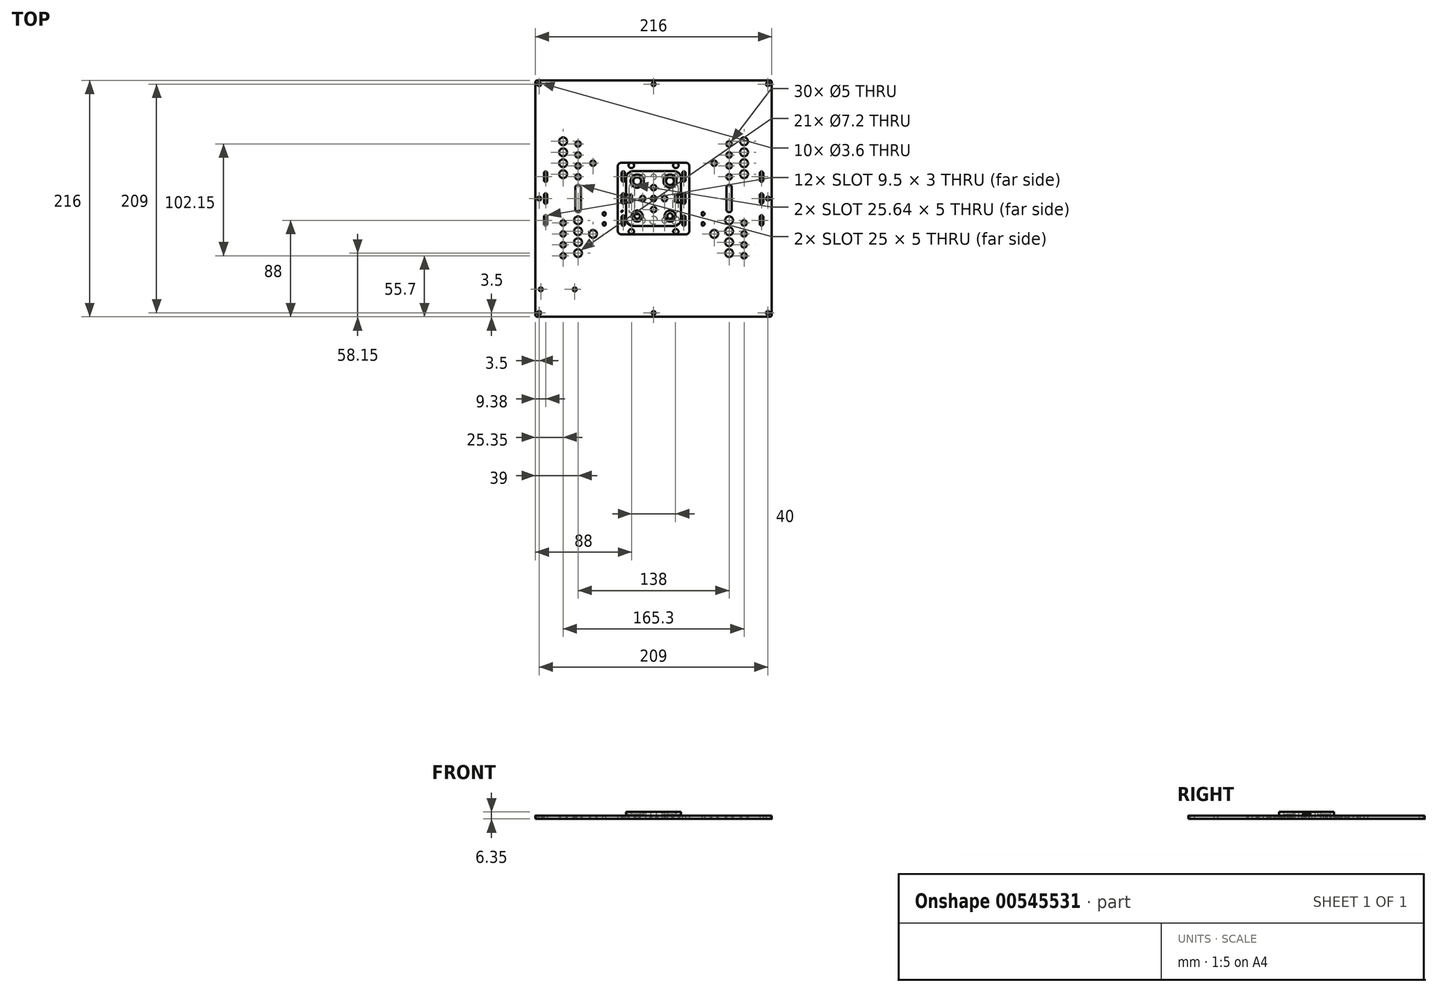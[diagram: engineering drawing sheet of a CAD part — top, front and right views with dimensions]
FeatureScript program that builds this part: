
annotation { "Feature Type Name" : "Feature", "Feature Type Description" : "" }
export const myFeature = defineFeature(function(context is Context, id is Id, definition is map)
    precondition{}
    {
        {
            var Q0;
            Q0=qCreatedBy(makeId("Top.planeOp"),FACE);
            var sketch = newSketch(context, id + "F0", { "sketchPlane" : qUnion([Q0])});
            skLineSegment(sketch, "E0.bottom", {"start": v(-106.25, 108) * mm, "end": v(106.25, 108) * mm});
            skLineSegment(sketch, "E0.top", {"start": v(-106.25, -108) * mm, "end": v(106.25, -108) * mm});
            skLineSegment(sketch, "E0.left", {"start": v(-108, 106.25) * mm, "end": v(-108, -106.25) * mm});
            skLineSegment(sketch, "E0.right", {"start": v(108, 106.25) * mm, "end": v(108, -106.25) * mm});
            skPoint(sketch, "E0.middle", {"position": v(0, 0) * mm});
            skPoint(sketch, "E1.visualSharp", {"position": v(-108, 108) * mm});
            skArc(sketch, "E1.filletArc", {"start": v(-106.25, 108) * mm, "mid": v(-107.49, 107.49) * mm, "end": v(-108, 106.25) * mm});
            skPoint(sketch, "E2.visualSharp", {"position": v(108, 108) * mm});
            skArc(sketch, "E2.filletArc", {"start": v(108, 106.25) * mm, "mid": v(107.49, 107.49) * mm, "end": v(106.25, 108) * mm});
            skPoint(sketch, "E3.visualSharp", {"position": v(108, -108) * mm});
            skArc(sketch, "E3.filletArc", {"start": v(106.25, -108) * mm, "mid": v(107.49, -107.49) * mm, "end": v(108, -106.25) * mm});
            skPoint(sketch, "E4.visualSharp", {"position": v(-108, -108) * mm});
            skArc(sketch, "E4.filletArc", {"start": v(-108, -106.25) * mm, "mid": v(-107.49, -107.49) * mm, "end": v(-106.25, -108) * mm});
            skCircle(sketch, "E5", {"center": v(-104.5, -104.5) * mm, "radius": 1.8 * mm});
            skCircle(sketch, "E6.0.1.0", {"center": v(-104.5, 0) * mm, "radius": 1.8 * mm});
            skCircle(sketch, "E6.0.2.0", {"center": v(-104.5, 104.5) * mm, "radius": 1.8 * mm});
            skCircle(sketch, "E6.1.0.0", {"center": v(0, -104.5) * mm, "radius": 1.8 * mm});
            skCircle(sketch, "E6.1.1.0", {"center": v(0, 0) * mm, "radius": 1.8 * mm});
            skCircle(sketch, "E6.1.2.0", {"center": v(0, 104.5) * mm, "radius": 1.8 * mm});
            skCircle(sketch, "E6.2.0.0", {"center": v(104.5, -104.5) * mm, "radius": 1.8 * mm});
            skCircle(sketch, "E6.2.1.0", {"center": v(104.5, 0) * mm, "radius": 1.8 * mm});
            skCircle(sketch, "E6.2.2.0", {"center": v(104.5, 104.5) * mm, "radius": 1.8 * mm});
            skLineSegment(sketch, "E6.direction1", {"start": v(-104.5, -104.5) * mm, "end": v(0, -104.5) * mm, "construction": true});
            skLineSegment(sketch, "E6.direction2", {"start": v(-104.5, -104.5) * mm, "end": v(-104.5, 0) * mm, "construction": true});
            skLineSegment(sketch, "E7", {"start": v(0, 0) * mm, "end": v(-30, 0) * mm, "construction": true});
            skLineSegment(sketch, "E8", {"start": v(0, 0) * mm, "end": v(0, -30) * mm, "construction": true});
            skCircle(sketch, "E9", {"center": v(-69, 19.85) * mm, "radius": 2.5 * mm});
            skCircle(sketch, "E10", {"center": v(-69, -19.85) * mm, "radius": 3.6 * mm});
            skLineSegment(sketch, "E11", {"start": v(-69, -19.85) * mm, "end": v(-69, 19.85) * mm, "construction": true});
            skPoint(sketch, "E12", {"position": v(-69, 0) * mm});
            skCircle(sketch, "E13.0.1.0", {"center": v(-69, 29.85) * mm, "radius": 2.5 * mm});
            skCircle(sketch, "E13.0.2.0", {"center": v(-69, 39.85) * mm, "radius": 2.5 * mm});
            skCircle(sketch, "E13.0.3.0", {"center": v(-69, 49.85) * mm, "radius": 2.5 * mm});
            skLineSegment(sketch, "E13.direction1", {"start": v(-69, 19.85) * mm, "end": v(-44, 19.85) * mm, "construction": true});
            skLineSegment(sketch, "E13.direction2", {"start": v(-69, 19.85) * mm, "end": v(-69, 29.85) * mm, "construction": true});
            skCircle(sketch, "E14.0.1.0", {"center": v(-69, -29.85) * mm, "radius": 3.6 * mm});
            skCircle(sketch, "E14.0.2.0", {"center": v(-69, -39.85) * mm, "radius": 3.6 * mm});
            skCircle(sketch, "E14.0.3.0", {"center": v(-69, -49.85) * mm, "radius": 3.6 * mm});
            skLineSegment(sketch, "E14.direction1", {"start": v(-69, -19.85) * mm, "end": v(-44, -19.85) * mm, "construction": true});
            skLineSegment(sketch, "E14.direction2", {"start": v(-69, -19.85) * mm, "end": v(-69, -29.85) * mm, "construction": true});
            skLineSegment(sketch, "E15", {"start": v(-82.65, 22.3) * mm, "end": v(-82.65, -22.3) * mm, "construction": true});
            skPoint(sketch, "E16", {"position": v(-82.65, 0) * mm});
            skCircle(sketch, "E17", {"center": v(-82.65, 22.3) * mm, "radius": 3.6 * mm});
            skCircle(sketch, "E18", {"center": v(-82.65, -22.3) * mm, "radius": 2.5 * mm});
            skCircle(sketch, "E19.0.1.0", {"center": v(-82.65, 32.3) * mm, "radius": 3.6 * mm});
            skCircle(sketch, "E19.0.2.0", {"center": v(-82.65, 42.3) * mm, "radius": 3.6 * mm});
            skCircle(sketch, "E19.0.3.0", {"center": v(-82.65, 52.3) * mm, "radius": 3.6 * mm});
            skLineSegment(sketch, "E19.direction1", {"start": v(-82.65, 22.3) * mm, "end": v(-57.65, 22.3) * mm, "construction": true});
            skLineSegment(sketch, "E19.direction2", {"start": v(-82.65, 22.3) * mm, "end": v(-82.65, 32.3) * mm, "construction": true});
            skCircle(sketch, "E20.0.1.0", {"center": v(-82.65, -32.3) * mm, "radius": 2.5 * mm});
            skCircle(sketch, "E20.0.2.0", {"center": v(-82.65, -42.3) * mm, "radius": 2.5 * mm});
            skCircle(sketch, "E20.0.3.0", {"center": v(-82.65, -52.3) * mm, "radius": 2.5 * mm});
            skLineSegment(sketch, "E20.direction1", {"start": v(-82.65, -22.3) * mm, "end": v(-57.65, -22.3) * mm, "construction": true});
            skLineSegment(sketch, "E20.direction2", {"start": v(-82.65, -22.3) * mm, "end": v(-82.65, -32.3) * mm, "construction": true});
            skLineSegment(sketch, "E21.MirrorCS", {"start": v(82.65, -22.3) * mm, "end": v(82.65, -32.3) * mm, "construction": true});
            skCircle(sketch, "E22.MirrorC", {"center": v(82.65, -32.3) * mm, "radius": 2.5 * mm});
            skCircle(sketch, "E23.MirrorC", {"center": v(69, 49.85) * mm, "radius": 2.5 * mm});
            skCircle(sketch, "E24.MirrorC", {"center": v(82.65, 22.3) * mm, "radius": 3.6 * mm});
            skLineSegment(sketch, "E25.MirrorCS", {"start": v(82.65, 22.3) * mm, "end": v(82.65, -22.3) * mm, "construction": true});
            skCircle(sketch, "E26.MirrorC", {"center": v(69, -49.85) * mm, "radius": 3.6 * mm});
            skCircle(sketch, "E27.MirrorC", {"center": v(82.65, 42.3) * mm, "radius": 3.6 * mm});
            skCircle(sketch, "E28.MirrorC", {"center": v(69, -19.85) * mm, "radius": 3.6 * mm});
            skCircle(sketch, "E29.MirrorC", {"center": v(69, 39.85) * mm, "radius": 2.5 * mm});
            skLineSegment(sketch, "E30.MirrorCS", {"start": v(82.65, 22.3) * mm, "end": v(82.65, 32.3) * mm, "construction": true});
            skCircle(sketch, "E31.MirrorC", {"center": v(69, 19.85) * mm, "radius": 2.5 * mm});
            skPoint(sketch, "E32.MirrorP", {"position": v(82.65, 0) * mm});
            skLineSegment(sketch, "E33.MirrorCS", {"start": v(69, -19.85) * mm, "end": v(69, -29.85) * mm, "construction": true});
            skCircle(sketch, "E34.MirrorC", {"center": v(69, 29.85) * mm, "radius": 2.5 * mm});
            skPoint(sketch, "E35.MirrorP", {"position": v(69, 0) * mm});
            skLineSegment(sketch, "E36.MirrorCS", {"start": v(69, -19.85) * mm, "end": v(69, 19.85) * mm, "construction": true});
            skCircle(sketch, "E37.MirrorC", {"center": v(69, -39.85) * mm, "radius": 3.6 * mm});
            skCircle(sketch, "E38.MirrorC", {"center": v(82.65, 52.3) * mm, "radius": 3.6 * mm});
            skCircle(sketch, "E39.MirrorC", {"center": v(82.65, -52.3) * mm, "radius": 2.5 * mm});
            skCircle(sketch, "E40.MirrorC", {"center": v(82.65, 32.3) * mm, "radius": 3.6 * mm});
            skCircle(sketch, "E41.MirrorC", {"center": v(82.65, -42.3) * mm, "radius": 2.5 * mm});
            skCircle(sketch, "E42.MirrorC", {"center": v(82.65, -22.3) * mm, "radius": 2.5 * mm});
            skCircle(sketch, "E43.MirrorC", {"center": v(69, -29.85) * mm, "radius": 3.6 * mm});
            skLineSegment(sketch, "E44.MirrorCS", {"start": v(69, 19.85) * mm, "end": v(69, 29.85) * mm, "construction": true});
            skCircle(sketch, "E45", {"center": v(0, 10) * mm, "radius": 2.5 * mm});
            skCircle(sketch, "E46", {"center": v(-10.16, 20.32) * mm, "radius": 2.5 * mm});
            skCircle(sketch, "E47", {"center": v(-20.33, 30.32) * mm, "radius": 2.5 * mm});
            skCircle(sketch, "E48.MirrorC", {"center": v(10.16, 20.32) * mm, "radius": 2.5 * mm});
            skCircle(sketch, "E49.MirrorC", {"center": v(20.33, 30.32) * mm, "radius": 2.5 * mm});
            skCircle(sketch, "E50.MirrorC", {"center": v(0, -10) * mm, "radius": 2.5 * mm});
            skCircle(sketch, "E51.MirrorC", {"center": v(-10.16, -20.32) * mm, "radius": 2.5 * mm});
            skCircle(sketch, "E52.MirrorC", {"center": v(10.16, -20.32) * mm, "radius": 2.5 * mm});
            skCircle(sketch, "E53.MirrorC", {"center": v(20.33, -30.32) * mm, "radius": 2.5 * mm});
            skCircle(sketch, "E54.MirrorC", {"center": v(-20.33, -30.32) * mm, "radius": 2.5 * mm});
            skCircle(sketch, "E55", {"center": v(-55.35, -32.3) * mm, "radius": 3.6 * mm});
            skCircle(sketch, "E56.MirrorC", {"center": v(55.35, -32.3) * mm, "radius": 3.6 * mm});
            skCircle(sketch, "E57", {"center": v(-55.35, 32.3) * mm, "radius": 2.5 * mm});
            skCircle(sketch, "E58.MirrorC", {"center": v(55.35, 32.3) * mm, "radius": 2.5 * mm});
            skLineSegment(sketch, "E59", {"start": v(-69, -10) * mm, "end": v(-69, 10) * mm, "construction": true});
            skArc(sketch, "E60.0.startCap", {"start": v(-66.5, -10) * mm, "mid": v(-69, -12.5) * mm, "end": v(-71.5, -10) * mm});
            skArc(sketch, "E60.0.endCap", {"start": v(-71.5, 10) * mm, "mid": v(-69, 12.5) * mm, "end": v(-66.5, 10) * mm});
            skLineSegment(sketch, "E60.0.left", {"start": v(-71.5, -10) * mm, "end": v(-71.5, 10) * mm});
            skLineSegment(sketch, "E60.0.right", {"start": v(-66.5, -10) * mm, "end": v(-66.5, 10) * mm});
            skLineSegment(sketch, "E61", {"start": v(-98.62, -16.75) * mm, "end": v(-98.62, -23.25) * mm, "construction": true});
            skArc(sketch, "E62.0.startCap", {"start": v(-100.12, -16.75) * mm, "mid": v(-98.62, -15.25) * mm, "end": v(-97.12, -16.75) * mm});
            skArc(sketch, "E62.0.endCap", {"start": v(-97.12, -23.25) * mm, "mid": v(-98.62, -24.75) * mm, "end": v(-100.12, -23.25) * mm});
            skLineSegment(sketch, "E62.0.left", {"start": v(-97.12, -16.75) * mm, "end": v(-97.12, -23.25) * mm});
            skLineSegment(sketch, "E62.0.right", {"start": v(-100.12, -16.75) * mm, "end": v(-100.12, -23.25) * mm});
            skLineSegment(sketch, "E63.0.1.0", {"start": v(-97.12, 3.25) * mm, "end": v(-97.12, -3.25) * mm});
            skArc(sketch, "E63.0.1.1", {"start": v(-100.12, 3.25) * mm, "mid": v(-98.62, 4.75) * mm, "end": v(-97.12, 3.25) * mm});
            skLineSegment(sketch, "E63.0.1.2", {"start": v(-100.12, 3.25) * mm, "end": v(-100.12, -3.25) * mm});
            skArc(sketch, "E63.0.1.3", {"start": v(-97.12, -3.25) * mm, "mid": v(-98.62, -4.75) * mm, "end": v(-100.12, -3.25) * mm});
            skLineSegment(sketch, "E63.0.2.0", {"start": v(-97.12, 23.25) * mm, "end": v(-97.12, 16.75) * mm});
            skArc(sketch, "E63.0.2.1", {"start": v(-100.12, 23.25) * mm, "mid": v(-98.62, 24.75) * mm, "end": v(-97.12, 23.25) * mm});
            skLineSegment(sketch, "E63.0.2.2", {"start": v(-100.12, 23.25) * mm, "end": v(-100.12, 16.75) * mm});
            skArc(sketch, "E63.0.2.3", {"start": v(-97.12, 16.75) * mm, "mid": v(-98.62, 15.25) * mm, "end": v(-100.12, 16.75) * mm});
            skLineSegment(sketch, "E63.direction1", {"start": v(-97.12, -23.25) * mm, "end": v(-88.77, -23.25) * mm, "construction": true});
            skLineSegment(sketch, "E63.direction2", {"start": v(-97.12, -23.25) * mm, "end": v(-97.12, -3.25) * mm, "construction": true});
            skLineSegment(sketch, "E64", {"start": v(-98.62, 3.25) * mm, "end": v(-98.62, -3.25) * mm, "construction": true});
            skPoint(sketch, "E65", {"position": v(-98.62, 0) * mm});
            skLineSegment(sketch, "E66.MirrorCS", {"start": v(97.12, -16.75) * mm, "end": v(97.12, -23.25) * mm});
            skLineSegment(sketch, "E67.MirrorCS", {"start": v(97.12, 23.25) * mm, "end": v(97.12, 16.75) * mm});
            skArc(sketch, "E68.MirrorCS", {"start": v(100.12, -16.75) * mm, "mid": v(98.62, -15.25) * mm, "end": v(97.12, -16.75) * mm});
            skArc(sketch, "E69.MirrorCS", {"start": v(97.12, -23.25) * mm, "mid": v(98.62, -24.75) * mm, "end": v(100.12, -23.25) * mm});
            skArc(sketch, "E70.MirrorCS", {"start": v(97.12, -3.25) * mm, "mid": v(98.62, -4.75) * mm, "end": v(100.12, -3.25) * mm});
            skArc(sketch, "E71.MirrorCS", {"start": v(100.12, 23.25) * mm, "mid": v(98.62, 24.75) * mm, "end": v(97.12, 23.25) * mm});
            skLineSegment(sketch, "E72.MirrorCS", {"start": v(97.12, 3.25) * mm, "end": v(97.12, -3.25) * mm});
            skArc(sketch, "E73.MirrorCS", {"start": v(97.12, 16.75) * mm, "mid": v(98.62, 15.25) * mm, "end": v(100.12, 16.75) * mm});
            skLineSegment(sketch, "E74.MirrorCS", {"start": v(100.12, 3.25) * mm, "end": v(100.12, -3.25) * mm});
            skArc(sketch, "E75.MirrorCS", {"start": v(100.12, 3.25) * mm, "mid": v(98.62, 4.75) * mm, "end": v(97.12, 3.25) * mm});
            skLineSegment(sketch, "E76.MirrorCS", {"start": v(100.12, 23.25) * mm, "end": v(100.12, 16.75) * mm});
            skLineSegment(sketch, "E77.MirrorCS", {"start": v(100.12, -16.75) * mm, "end": v(100.12, -23.25) * mm});
            skCircle(sketch, "E78", {"center": v(-103, -83) * mm, "radius": 1.8 * mm});
            skCircle(sketch, "E79", {"center": v(-72, -83) * mm, "radius": 1.8 * mm});
            skCircle(sketch, "E80", {"center": v(-15.17, -12.64) * mm, "radius": 1.75 * mm});
            skCircle(sketch, "E81.0.1.0", {"center": v(-15.17, -2.5) * mm, "radius": 1.75 * mm});
            skCircle(sketch, "E81.1.0.0", {"center": v(-28, -12.64) * mm, "radius": 1.75 * mm});
            skCircle(sketch, "E81.1.1.0", {"center": v(-28, -2.5) * mm, "radius": 1.75 * mm});
            skLineSegment(sketch, "E81.direction1", {"start": v(-15.17, -12.64) * mm, "end": v(-28, -12.64) * mm, "construction": true});
            skLineSegment(sketch, "E81.direction2", {"start": v(-15.17, -12.64) * mm, "end": v(-15.17, -2.5) * mm, "construction": true});
            skCircle(sketch, "E82", {"center": v(-45, -14) * mm, "radius": 1.57 * mm});
            skCircle(sketch, "E83", {"center": v(-45, -23.12) * mm, "radius": 1.57 * mm});
            skCircle(sketch, "E84.MirrorC", {"center": v(45, -23.12) * mm, "radius": 1.57 * mm});
            skCircle(sketch, "E85.MirrorC", {"center": v(45, -14) * mm, "radius": 1.57 * mm});
            skArc(sketch, "E86.MirrorCS", {"start": v(66.5, -10) * mm, "mid": v(69, -12.5) * mm, "end": v(71.5, -10) * mm});
            skArc(sketch, "E87.MirrorCS", {"start": v(71.5, 10) * mm, "mid": v(69, 12.5) * mm, "end": v(66.5, 10) * mm});
            skLineSegment(sketch, "E88.MirrorCS", {"start": v(69, -10) * mm, "end": v(69, 10) * mm, "construction": true});
            skLineSegment(sketch, "E89.MirrorCS", {"start": v(71.5, -10) * mm, "end": v(71.5, 10) * mm});
            skLineSegment(sketch, "E90.MirrorCS", {"start": v(66.5, -10) * mm, "end": v(66.5, 10) * mm});
            skSolve(sketch);
        }
        {
            var Q0;
            Q0=makeQuery(id+"F0.imprint","IMPRINT",FACE,{"disambiguationData":[TD([[makeQuery(id+"F0.imprint","IMPRINT",EDGE,{"derivedFrom":sQuery(id+"F0.wireOp",EDGE,"E0.bottom")}),-1.0]])]});
            extrude(context, id + "F1", {"entities" : qUnion([Q0]), "depth" : 3 * mm, "offsetDistance" : 25 * mm});
        }
        {
            var Q0;
            Q0=qCreatedBy(makeId("Top.planeOp"),FACE);
            var sketch = newSketch(context, id + "F2", { "sketchPlane" : qUnion([Q0])});
            skLineSegment(sketch, "E91.bottom", {"start": v(-41, 63.5) * mm, "end": v(41, 63.5) * mm});
            skLineSegment(sketch, "E91.top", {"start": v(-41, -63.5) * mm, "end": v(41, -63.5) * mm});
            skLineSegment(sketch, "E91.left", {"start": v(-44, 60.5) * mm, "end": v(-44, -60.5) * mm});
            skLineSegment(sketch, "E91.right", {"start": v(44, 60.5) * mm, "end": v(44, -60.5) * mm});
            skPoint(sketch, "E91.middle", {"position": v(0, 0) * mm});
            skLineSegment(sketch, "E92.MirrorCS", {"start": v(36.5, -16.75) * mm, "end": v(36.5, -23.25) * mm});
            skArc(sketch, "E93.MirrorCS", {"start": v(39.5, -16.75) * mm, "mid": v(38, -15.25) * mm, "end": v(36.5, -16.75) * mm});
            skArc(sketch, "E94.MirrorCS", {"start": v(36.5, -23.25) * mm, "mid": v(38, -24.75) * mm, "end": v(39.5, -23.25) * mm});
            skLineSegment(sketch, "E95.MirrorCS", {"start": v(39.5, -16.75) * mm, "end": v(39.5, -23.25) * mm});
            skLineSegment(sketch, "E96.0.1.0", {"start": v(39.5, 3.25) * mm, "end": v(39.5, -3.25) * mm});
            skLineSegment(sketch, "E96.0.1.1", {"start": v(36.5, 3.25) * mm, "end": v(36.5, -3.25) * mm});
            skArc(sketch, "E96.0.1.2", {"start": v(39.5, 3.25) * mm, "mid": v(38, 4.75) * mm, "end": v(36.5, 3.25) * mm});
            skArc(sketch, "E96.0.1.3", {"start": v(36.5, -3.25) * mm, "mid": v(38, -4.75) * mm, "end": v(39.5, -3.25) * mm});
            skLineSegment(sketch, "E96.0.2.0", {"start": v(39.5, 23.25) * mm, "end": v(39.5, 16.75) * mm});
            skLineSegment(sketch, "E96.0.2.1", {"start": v(36.5, 23.25) * mm, "end": v(36.5, 16.75) * mm});
            skArc(sketch, "E96.0.2.2", {"start": v(39.5, 23.25) * mm, "mid": v(38, 24.75) * mm, "end": v(36.5, 23.25) * mm});
            skArc(sketch, "E96.0.2.3", {"start": v(36.5, 16.75) * mm, "mid": v(38, 15.25) * mm, "end": v(39.5, 16.75) * mm});
            skLineSegment(sketch, "E96.direction1", {"start": v(36.5, -23.25) * mm, "end": v(59.96, -23.25) * mm, "construction": true});
            skLineSegment(sketch, "E96.direction2", {"start": v(36.5, -23.25) * mm, "end": v(36.5, -3.25) * mm, "construction": true});
            skLineSegment(sketch, "E97", {"start": v(39.5, 0) * mm, "end": v(44, 0) * mm, "construction": true});
            skLineSegment(sketch, "E98", {"start": v(0, 0) * mm, "end": v(0, 10) * mm, "construction": true});
            skLineSegment(sketch, "E99", {"start": v(0, 0) * mm, "end": v(-10, 0) * mm, "construction": true});
            skLineSegment(sketch, "E100.MirrorCS", {"start": v(-36.5, -16.75) * mm, "end": v(-36.5, -23.25) * mm});
            skArc(sketch, "E101.MirrorCS", {"start": v(-36.5, -23.25) * mm, "mid": v(-38, -24.75) * mm, "end": v(-39.5, -23.25) * mm});
            skLineSegment(sketch, "E102.MirrorCS", {"start": v(-39.5, -16.75) * mm, "end": v(-39.5, -23.25) * mm});
            skArc(sketch, "E103.MirrorCS", {"start": v(-39.5, -16.75) * mm, "mid": v(-38, -15.25) * mm, "end": v(-36.5, -16.75) * mm});
            skArc(sketch, "E104.MirrorCS", {"start": v(-36.5, 16.75) * mm, "mid": v(-38, 15.25) * mm, "end": v(-39.5, 16.75) * mm});
            skLineSegment(sketch, "E105.MirrorCS", {"start": v(-39.5, 3.25) * mm, "end": v(-39.5, -3.25) * mm});
            skArc(sketch, "E106.MirrorCS", {"start": v(-39.5, 23.25) * mm, "mid": v(-38, 24.75) * mm, "end": v(-36.5, 23.25) * mm});
            skLineSegment(sketch, "E107.MirrorCS", {"start": v(-36.5, 3.25) * mm, "end": v(-36.5, -3.25) * mm});
            skArc(sketch, "E108.MirrorCS", {"start": v(-39.5, 3.25) * mm, "mid": v(-38, 4.75) * mm, "end": v(-36.5, 3.25) * mm});
            skArc(sketch, "E109.MirrorCS", {"start": v(-36.5, -3.25) * mm, "mid": v(-38, -4.75) * mm, "end": v(-39.5, -3.25) * mm});
            skLineSegment(sketch, "E110.MirrorCS", {"start": v(-39.5, 23.25) * mm, "end": v(-39.5, 16.75) * mm});
            skLineSegment(sketch, "E111.MirrorCS", {"start": v(-36.5, 23.25) * mm, "end": v(-36.5, 16.75) * mm});
            skLineSegment(sketch, "E112", {"start": v(30.32, -10) * mm, "end": v(30.32, 10) * mm, "construction": true});
            skPoint(sketch, "E113", {"position": v(30.32, 0) * mm});
            skArc(sketch, "E114.0.startCap", {"start": v(32.82, -10) * mm, "mid": v(30.32, -12.5) * mm, "end": v(27.82, -10) * mm});
            skArc(sketch, "E114.0.endCap", {"start": v(27.82, 10) * mm, "mid": v(30.32, 12.5) * mm, "end": v(32.82, 10) * mm});
            skLineSegment(sketch, "E114.0.left", {"start": v(27.82, -10) * mm, "end": v(27.82, 10) * mm});
            skLineSegment(sketch, "E114.0.right", {"start": v(32.82, -10) * mm, "end": v(32.82, 10) * mm});
            skLineSegment(sketch, "E115", {"start": v(44, 0) * mm, "end": v(30.32, 0) * mm, "construction": true});
            skLineSegment(sketch, "E116.MirrorCS", {"start": v(-27.82, -10) * mm, "end": v(-27.82, 10) * mm});
            skPoint(sketch, "E117.MirrorP", {"position": v(-30.32, 0) * mm});
            skLineSegment(sketch, "E118.MirrorCS", {"start": v(-30.32, -10) * mm, "end": v(-30.32, 10) * mm, "construction": true});
            skArc(sketch, "E119.MirrorCS", {"start": v(-32.82, -10) * mm, "mid": v(-30.32, -12.5) * mm, "end": v(-27.82, -10) * mm});
            skArc(sketch, "E120.MirrorCS", {"start": v(-27.82, 10) * mm, "mid": v(-30.32, 12.5) * mm, "end": v(-32.82, 10) * mm});
            skLineSegment(sketch, "E121.MirrorCS", {"start": v(-32.82, -10) * mm, "end": v(-32.82, 10) * mm});
            skCircle(sketch, "E122", {"center": v(-30.32, -19.85) * mm, "radius": 3.55 * mm});
            skCircle(sketch, "E123", {"center": v(-30.32, 19.85) * mm, "radius": 2.55 * mm});
            skLineSegment(sketch, "E124", {"start": v(-30.32, -19.85) * mm, "end": v(-30.32, 19.85) * mm, "construction": true});
            skCircle(sketch, "E125.0.1.0", {"center": v(-30.32, -29.85) * mm, "radius": 3.55 * mm});
            skCircle(sketch, "E125.0.2.0", {"center": v(-30.32, -39.85) * mm, "radius": 3.55 * mm});
            skCircle(sketch, "E125.0.3.0", {"center": v(-30.32, -49.85) * mm, "radius": 3.55 * mm});
            skCircle(sketch, "E125.1.0.0", {"center": v(0, -19.85) * mm, "radius": 3.55 * mm});
            skCircle(sketch, "E125.1.1.0", {"center": v(0, -29.85) * mm, "radius": 3.55 * mm});
            skCircle(sketch, "E125.1.2.0", {"center": v(0, -39.85) * mm, "radius": 3.55 * mm});
            skCircle(sketch, "E125.1.3.0", {"center": v(0, -49.85) * mm, "radius": 3.55 * mm});
            skCircle(sketch, "E125.2.0.0", {"center": v(30.32, -19.85) * mm, "radius": 3.55 * mm});
            skCircle(sketch, "E125.2.1.0", {"center": v(30.32, -29.85) * mm, "radius": 3.55 * mm});
            skCircle(sketch, "E125.2.2.0", {"center": v(30.32, -39.85) * mm, "radius": 3.55 * mm});
            skCircle(sketch, "E125.2.3.0", {"center": v(30.32, -49.85) * mm, "radius": 3.55 * mm});
            skLineSegment(sketch, "E125.direction1", {"start": v(-30.32, -19.85) * mm, "end": v(0, -19.85) * mm, "construction": true});
            skLineSegment(sketch, "E125.direction2", {"start": v(-30.32, -19.85) * mm, "end": v(-30.32, -29.85) * mm, "construction": true});
            skCircle(sketch, "E126.0.1.0", {"center": v(-30.32, 29.85) * mm, "radius": 2.55 * mm});
            skCircle(sketch, "E126.0.2.0", {"center": v(-30.32, 39.85) * mm, "radius": 2.55 * mm});
            skCircle(sketch, "E126.0.3.0", {"center": v(-30.32, 49.85) * mm, "radius": 2.55 * mm});
            skCircle(sketch, "E126.1.0.0", {"center": v(0, 19.85) * mm, "radius": 2.55 * mm});
            skCircle(sketch, "E126.1.1.0", {"center": v(0, 29.85) * mm, "radius": 2.55 * mm});
            skCircle(sketch, "E126.1.2.0", {"center": v(0, 39.85) * mm, "radius": 2.55 * mm});
            skCircle(sketch, "E126.1.3.0", {"center": v(0, 49.85) * mm, "radius": 2.55 * mm});
            skCircle(sketch, "E126.2.0.0", {"center": v(30.32, 19.85) * mm, "radius": 2.55 * mm});
            skCircle(sketch, "E126.2.1.0", {"center": v(30.32, 29.85) * mm, "radius": 2.55 * mm});
            skCircle(sketch, "E126.2.2.0", {"center": v(30.32, 39.85) * mm, "radius": 2.55 * mm});
            skCircle(sketch, "E126.2.3.0", {"center": v(30.32, 49.85) * mm, "radius": 2.55 * mm});
            skLineSegment(sketch, "E126.direction1", {"start": v(-30.32, 19.85) * mm, "end": v(0, 19.85) * mm, "construction": true});
            skLineSegment(sketch, "E126.direction2", {"start": v(-30.32, 19.85) * mm, "end": v(-30.32, 29.85) * mm, "construction": true});
            skCircle(sketch, "E127", {"center": v(-20.32, -49.85) * mm, "radius": 2.55 * mm});
            skCircle(sketch, "E128.0.1.0", {"center": v(-20.32, -39.85) * mm, "radius": 2.55 * mm});
            skCircle(sketch, "E128.0.2.0", {"center": v(-20.32, -29.85) * mm, "radius": 2.55 * mm});
            skCircle(sketch, "E128.0.3.0", {"center": v(-20.32, -19.85) * mm, "radius": 2.55 * mm});
            skCircle(sketch, "E128.0.4.0", {"center": v(-20.32, -9.85) * mm, "radius": 2.55 * mm});
            skCircle(sketch, "E128.0.5.0", {"center": v(-20.32, 0.15) * mm, "radius": 2.55 * mm});
            skCircle(sketch, "E128.0.6.0", {"center": v(-20.32, 10.15) * mm, "radius": 2.55 * mm});
            skCircle(sketch, "E128.0.7.0", {"center": v(-20.32, 20.15) * mm, "radius": 2.55 * mm});
            skCircle(sketch, "E128.0.8.0", {"center": v(-20.32, 30.15) * mm, "radius": 2.55 * mm});
            skCircle(sketch, "E128.0.9.0", {"center": v(-20.32, 40.15) * mm, "radius": 2.55 * mm});
            skCircle(sketch, "E128.0.10.0", {"center": v(-20.32, 50.15) * mm, "radius": 2.55 * mm});
            skCircle(sketch, "E128.1.0.0", {"center": v(20.32, -49.85) * mm, "radius": 2.55 * mm});
            skCircle(sketch, "E128.1.1.0", {"center": v(20.32, -39.85) * mm, "radius": 2.55 * mm});
            skCircle(sketch, "E128.1.2.0", {"center": v(20.32, -29.85) * mm, "radius": 2.55 * mm});
            skCircle(sketch, "E128.1.3.0", {"center": v(20.32, -19.85) * mm, "radius": 2.55 * mm});
            skCircle(sketch, "E128.1.4.0", {"center": v(20.32, -9.85) * mm, "radius": 2.55 * mm});
            skCircle(sketch, "E128.1.5.0", {"center": v(20.32, 0.15) * mm, "radius": 2.55 * mm});
            skCircle(sketch, "E128.1.6.0", {"center": v(20.32, 10.15) * mm, "radius": 2.55 * mm});
            skCircle(sketch, "E128.1.7.0", {"center": v(20.32, 20.15) * mm, "radius": 2.55 * mm});
            skCircle(sketch, "E128.1.8.0", {"center": v(20.32, 30.15) * mm, "radius": 2.55 * mm});
            skCircle(sketch, "E128.1.9.0", {"center": v(20.32, 40.15) * mm, "radius": 2.55 * mm});
            skCircle(sketch, "E128.1.10.0", {"center": v(20.32, 50.15) * mm, "radius": 2.55 * mm});
            skLineSegment(sketch, "E128.direction1", {"start": v(-20.32, -49.85) * mm, "end": v(20.32, -49.85) * mm, "construction": true});
            skLineSegment(sketch, "E128.direction2", {"start": v(-20.32, -49.85) * mm, "end": v(-20.32, -39.85) * mm, "construction": true});
            skLineSegment(sketch, "E129", {"start": v(20.32, -49.85) * mm, "end": v(30.32, -49.85) * mm, "construction": true});
            skCircle(sketch, "E130", {"center": v(0, 0) * mm, "radius": 2.55 * mm});
            skCircle(sketch, "E131", {"center": v(0, 10) * mm, "radius": 2.55 * mm});
            skCircle(sketch, "E132.1.1", {"center": v(-10, 0) * mm, "radius": 2.55 * mm});
            skCircle(sketch, "E132.2.1", {"center": v(0, -10) * mm, "radius": 2.55 * mm});
            skCircle(sketch, "E132.3.1", {"center": v(10, 0) * mm, "radius": 2.55 * mm});
            skCircle(sketch, "E133.1.1", {"center": v(-10, 20.32) * mm, "radius": 2.55 * mm});
            skCircle(sketch, "E133.3.1", {"center": v(10, 20.32) * mm, "radius": 2.55 * mm});
            skCircle(sketch, "E134", {"center": v(-10, 30.32) * mm, "radius": 2.55 * mm});
            skCircle(sketch, "E135", {"center": v(10, 30.32) * mm, "radius": 2.55 * mm});
            skCircle(sketch, "E136.MirrorC", {"center": v(-10, -20.32) * mm, "radius": 2.55 * mm});
            skCircle(sketch, "E137.MirrorC", {"center": v(-10, -30.32) * mm, "radius": 2.55 * mm});
            skCircle(sketch, "E138.MirrorC", {"center": v(10, -30.32) * mm, "radius": 2.55 * mm});
            skCircle(sketch, "E139.MirrorC", {"center": v(10, -20.32) * mm, "radius": 2.55 * mm});
            skCircle(sketch, "E140", {"center": v(-14.82, -14.83) * mm, "radius": 2.55 * mm});
            skCircle(sketch, "E141.0.1.0", {"center": v(-14.82, 14.83) * mm, "radius": 2.55 * mm});
            skCircle(sketch, "E141.1.0.0", {"center": v(14.83, -14.82) * mm, "radius": 2.55 * mm});
            skCircle(sketch, "E141.1.1.0", {"center": v(14.82, 14.83) * mm, "radius": 2.55 * mm});
            skLineSegment(sketch, "E141.direction1", {"start": v(-14.82, -14.83) * mm, "end": v(14.83, -14.82) * mm, "construction": true});
            skLineSegment(sketch, "E141.direction2", {"start": v(-14.82, -14.83) * mm, "end": v(-14.82, 14.83) * mm, "construction": true});
            skPoint(sketch, "E142.visualSharp", {"position": v(-44, 63.5) * mm});
            skArc(sketch, "E142.filletArc", {"start": v(-41, 63.5) * mm, "mid": v(-43.12, 62.62) * mm, "end": v(-44, 60.5) * mm});
            skPoint(sketch, "E143.visualSharp", {"position": v(44, 63.5) * mm});
            skArc(sketch, "E143.filletArc", {"start": v(44, 60.5) * mm, "mid": v(43.12, 62.62) * mm, "end": v(41, 63.5) * mm});
            skPoint(sketch, "E144.visualSharp", {"position": v(44, -63.5) * mm});
            skArc(sketch, "E144.filletArc", {"start": v(41, -63.5) * mm, "mid": v(43.12, -62.62) * mm, "end": v(44, -60.5) * mm});
            skPoint(sketch, "E145.visualSharp", {"position": v(-44, -63.5) * mm});
            skArc(sketch, "E145.filletArc", {"start": v(-44, -60.5) * mm, "mid": v(-43.12, -62.62) * mm, "end": v(-41, -63.5) * mm});
            skSolve(sketch);
        }
        {
            var Q0;
            Q0=makeQuery(id+"F2.imprint","IMPRINT",FACE,{"disambiguationData":[TD([[makeQuery(id+"F2.imprint","IMPRINT",EDGE,{"derivedFrom":sQuery(id+"F2.wireOp",EDGE,"E91.bottom")}),-1.0]])]});
            extrude(context, id + "F3", {"entities" : qUnion([Q0]), "depth" : 3 * mm, "offsetDistance" : 25 * mm});
        }
        {
            assignVariable(context, id + "F4", {"name" : "miniVGantryPlateThickness", "anyValue" : 6.35});
        }
        {
            var Q0;
            Q0=qCreatedBy(makeId("Top.planeOp"),FACE);
            var sketch = newSketch(context, id + "F5", { "sketchPlane" : qUnion([Q0])});
            skLineSegment(sketch, "E146.bottom", {"start": v(18.83, -25) * mm, "end": v(-18.83, -25) * mm});
            skLineSegment(sketch, "E146.top", {"start": v(18.83, 25) * mm, "end": v(-18.83, 25) * mm});
            skLineSegment(sketch, "E146.left", {"start": v(25, -18.83) * mm, "end": v(25, 18.83) * mm});
            skLineSegment(sketch, "E146.right", {"start": v(-25, -18.83) * mm, "end": v(-25, 18.83) * mm});
            skPoint(sketch, "E146.middle", {"position": v(0, 0) * mm});
            skCircle(sketch, "E147", {"center": v(0, 0) * mm, "radius": 2.5 * mm});
            skCircle(sketch, "E148", {"center": v(0, 10) * mm, "radius": 2.5 * mm});
            skCircle(sketch, "E149.1.0", {"center": v(-10, 0) * mm, "radius": 2.5 * mm});
            skCircle(sketch, "E149.2.0", {"center": v(0, -10) * mm, "radius": 2.5 * mm});
            skCircle(sketch, "E149.3.0", {"center": v(10, 0) * mm, "radius": 2.5 * mm});
            skCircle(sketch, "E150", {"center": v(-15, 15.95) * mm, "radius": 3.57 * mm});
            skCircle(sketch, "E151", {"center": v(-15, 15.95) * mm, "radius": 6 * mm});
            skLineSegment(sketch, "E152", {"start": v(0, 0) * mm, "end": v(0, 25) * mm, "construction": true});
            skCircle(sketch, "E153.MirrorC", {"center": v(15, 15.95) * mm, "radius": 3.57 * mm});
            skCircle(sketch, "E154.MirrorC", {"center": v(15, 15.95) * mm, "radius": 6 * mm});
            skCircle(sketch, "E155", {"center": v(-15, -15.95) * mm, "radius": 2.5 * mm});
            skCircle(sketch, "E156", {"center": v(-15, -15.95) * mm, "radius": 5.05 * mm});
            skCircle(sketch, "E157.MirrorC", {"center": v(15, -15.95) * mm, "radius": 2.5 * mm});
            skCircle(sketch, "E158.MirrorC", {"center": v(15, -15.95) * mm, "radius": 5.05 * mm});
            skLineSegment(sketch, "E159", {"start": v(0, 0) * mm, "end": v(-25, 0) * mm, "construction": true});
            skPoint(sketch, "E160.visualSharp", {"position": v(-25, 25) * mm});
            skArc(sketch, "E160.filletArc", {"start": v(-18.83, 25) * mm, "mid": v(-23.2, 23.2) * mm, "end": v(-25, 18.83) * mm});
            skPoint(sketch, "E161.visualSharp", {"position": v(25, 25) * mm});
            skArc(sketch, "E161.filletArc", {"start": v(25, 18.83) * mm, "mid": v(23.2, 23.2) * mm, "end": v(18.83, 25) * mm});
            skPoint(sketch, "E162.visualSharp", {"position": v(25, -25) * mm});
            skArc(sketch, "E162.filletArc", {"start": v(18.83, -25) * mm, "mid": v(23.2, -23.2) * mm, "end": v(25, -18.83) * mm});
            skPoint(sketch, "E163.visualSharp", {"position": v(-25, -25) * mm});
            skArc(sketch, "E163.filletArc", {"start": v(-25, -18.83) * mm, "mid": v(-23.2, -23.2) * mm, "end": v(-18.83, -25) * mm});
            skLineSegment(sketch, "E164", {"start": v(-25, 3.35) * mm, "end": v(-19.75, 3.35) * mm});
            skLineSegment(sketch, "E165", {"start": v(-19.75, 3.35) * mm, "end": v(-19.75, -3.35) * mm});
            skLineSegment(sketch, "E166", {"start": v(-19.75, -3.35) * mm, "end": v(-25, -3.35) * mm});
            skLineSegment(sketch, "E167", {"start": v(-22.25, 3.35) * mm, "end": v(-22.25, -3.35) * mm});
            skLineSegment(sketch, "E168.MirrorCS", {"start": v(19.75, 3.35) * mm, "end": v(19.75, -3.35) * mm});
            skLineSegment(sketch, "E169.MirrorCS", {"start": v(25, 3.35) * mm, "end": v(19.75, 3.35) * mm});
            skLineSegment(sketch, "E170.MirrorCS", {"start": v(19.75, -3.35) * mm, "end": v(25, -3.35) * mm});
            skLineSegment(sketch, "E171.MirrorCS", {"start": v(22.25, 3.35) * mm, "end": v(22.25, -3.35) * mm});
            skSolve(sketch);
        }
        {
            var Q0;
            Q0=makeQuery(id+"F5.imprint","IMPRINT",FACE,{"disambiguationData":[TD([[makeQuery(id+"F5.imprint","IMPRINT",EDGE,{"derivedFrom":sQuery(id+"F5.wireOp",EDGE,"E146.bottom")}),-1.0]])]});
            extrude(context, id + "F6", {"entities" : qUnion([Q0]), "depth" : (getVariable(context, 'miniVGantryPlateThickness')) * mm, "offsetDistance" : 25 * mm});
        }
        {
            var Q0;
            Q0=makeQuery(id+"F5.imprint","IMPRINT",FACE,{"disambiguationData":[TD([[makeQuery(id+"F5.imprint","IMPRINT",EDGE,{"derivedFrom":sQuery(id+"F5.wireOp",EDGE,"E150")}),-1.0]])]});
            var Q1;
            Q1=makeQuery(id+"F5.imprint","IMPRINT",FACE,{"disambiguationData":[TD([[makeQuery(id+"F5.imprint","IMPRINT",EDGE,{"derivedFrom":sQuery(id+"F5.wireOp",EDGE,"E153.MirrorC")}),1.0]])]});
            var Q2;
            Q2=makeQuery(id+"F5.imprint","IMPRINT",FACE,{"disambiguationData":[TD([[makeQuery(id+"F5.imprint","IMPRINT",EDGE,{"derivedFrom":sQuery(id+"F5.wireOp",EDGE,"E157.MirrorC")}),1.0]])]});
            var Q3;
            Q3=makeQuery(id+"F5.imprint","IMPRINT",FACE,{"disambiguationData":[TD([[makeQuery(id+"F5.imprint","IMPRINT",EDGE,{"derivedFrom":sQuery(id+"F5.wireOp",EDGE,"E155")}),-1.0]])]});
            extrude(context, id + "F7", {"entities" : qUnion([Q0, Q1, Q2, Q3]), "operationType" : NewBodyOperationType.ADD, "depth" : (getVariable(context, 'miniVGantryPlateThickness') - 2) * mm, "offsetDistance" : 25 * mm});
        }
        {
            var Q0;
            {var subQ5=sQuery(id+"F5.wireOp",EDGE,"E167");Q0=makeQuery(id+"F5.imprint","IMPRINT",FACE,{"disambiguationData":[TD([[makeQuery(id+"F5.imprint","IMPRINT",EDGE,{"derivedFrom":subQ5}),-1.0]])]});}
            var Q1;
            {var subQ5=sQuery(id+"F5.wireOp",EDGE,"E171.MirrorCS");Q1=makeQuery(id+"F5.imprint","IMPRINT",FACE,{"disambiguationData":[TD([[makeQuery(id+"F5.imprint","IMPRINT",EDGE,{"derivedFrom":subQ5}),1.0]])]});}
            extrude(context, id + "F8", {"entities" : qUnion([Q0, Q1]), "operationType" : NewBodyOperationType.ADD, "depth" : (getVariable(context, 'miniVGantryPlateThickness') - 2.18) * mm, "offsetDistance" : 25 * mm});
        }
        {
            var Q0;
            Q0=qCreatedBy(makeId("Top.planeOp"),FACE);
            var sketch = newSketch(context, id + "F9", { "sketchPlane" : qUnion([Q0])});
            skLineSegment(sketch, "E172.bottom", {"start": v(-29.37, -32.75) * mm, "end": v(29.37, -32.75) * mm});
            skLineSegment(sketch, "E172.top", {"start": v(-29.37, 32.75) * mm, "end": v(29.37, 32.75) * mm});
            skLineSegment(sketch, "E172.left", {"start": v(-32.75, -29.37) * mm, "end": v(-32.75, 29.37) * mm});
            skLineSegment(sketch, "E172.right", {"start": v(32.75, -29.37) * mm, "end": v(32.75, 29.37) * mm});
            skLineSegment(sketch, "E173", {"start": v(0, 0) * mm, "end": v(-32.75, 0) * mm, "construction": true});
            skLineSegment(sketch, "E174", {"start": v(0, 0) * mm, "end": v(0, 32.75) * mm, "construction": true});
            skPoint(sketch, "E175.visualSharp", {"position": v(-32.75, 32.75) * mm});
            skArc(sketch, "E175.filletArc", {"start": v(-29.37, 32.75) * mm, "mid": v(-31.76, 31.76) * mm, "end": v(-32.75, 29.37) * mm});
            skPoint(sketch, "E176.visualSharp", {"position": v(32.75, 32.75) * mm});
            skArc(sketch, "E176.filletArc", {"start": v(32.75, 29.37) * mm, "mid": v(31.76, 31.76) * mm, "end": v(29.37, 32.75) * mm});
            skPoint(sketch, "E177.visualSharp", {"position": v(32.75, -32.75) * mm});
            skArc(sketch, "E177.filletArc", {"start": v(29.37, -32.75) * mm, "mid": v(31.76, -31.76) * mm, "end": v(32.75, -29.37) * mm});
            skPoint(sketch, "E178.visualSharp", {"position": v(-32.75, -32.75) * mm});
            skArc(sketch, "E178.filletArc", {"start": v(-32.75, -29.37) * mm, "mid": v(-31.76, -31.76) * mm, "end": v(-29.37, -32.75) * mm});
            skCircle(sketch, "E179", {"center": v(0, 0) * mm, "radius": 2.5 * mm});
            skCircle(sketch, "E180", {"center": v(0, 10) * mm, "radius": 2.5 * mm});
            skCircle(sketch, "E181.1.0", {"center": v(-10, 0) * mm, "radius": 2.5 * mm});
            skCircle(sketch, "E181.2.0", {"center": v(0, -10) * mm, "radius": 2.5 * mm});
            skCircle(sketch, "E181.3.0", {"center": v(10, 0) * mm, "radius": 2.5 * mm});
            skCircle(sketch, "E182", {"center": v(-20, 19.85) * mm, "radius": 2.5 * mm});
            skCircle(sketch, "E183.1.0.0", {"center": v(-10, 19.85) * mm, "radius": 2.5 * mm});
            skCircle(sketch, "E183.2.0.0", {"center": v(0, 19.85) * mm, "radius": 2.5 * mm});
            skCircle(sketch, "E183.3.0.0", {"center": v(10, 19.85) * mm, "radius": 2.5 * mm});
            skCircle(sketch, "E183.4.0.0", {"center": v(20, 19.85) * mm, "radius": 2.5 * mm});
            skLineSegment(sketch, "E183.direction1", {"start": v(-20, 19.85) * mm, "end": v(-10, 19.85) * mm, "construction": true});
            skCircle(sketch, "E184.MirrorC", {"center": v(-20, -19.85) * mm, "radius": 2.5 * mm, "construction": true});
            skCircle(sketch, "E185.MirrorC", {"center": v(-10, -19.85) * mm, "radius": 2.5 * mm});
            skCircle(sketch, "E186.MirrorC", {"center": v(0, -19.85) * mm, "radius": 2.5 * mm, "construction": true});
            skCircle(sketch, "E187.MirrorC", {"center": v(10, -19.85) * mm, "radius": 2.5 * mm});
            skCircle(sketch, "E188.MirrorC", {"center": v(20, -19.85) * mm, "radius": 2.5 * mm, "construction": true});
            skCircle(sketch, "E189", {"center": v(-20, -19.85) * mm, "radius": 3.6 * mm});
            skCircle(sketch, "E190", {"center": v(0, -19.85) * mm, "radius": 3.6 * mm});
            skCircle(sketch, "E191", {"center": v(20, -19.85) * mm, "radius": 3.6 * mm});
            skLineSegment(sketch, "E192", {"start": v(-20, 10.32) * mm, "end": v(-20, -10.32) * mm, "construction": true});
            skArc(sketch, "E193.0.startCap", {"start": v(-22.5, 10.32) * mm, "mid": v(-20, 12.82) * mm, "end": v(-17.5, 10.32) * mm});
            skArc(sketch, "E193.0.endCap", {"start": v(-17.5, -10.32) * mm, "mid": v(-20, -12.82) * mm, "end": v(-22.5, -10.32) * mm});
            skLineSegment(sketch, "E193.0.left", {"start": v(-17.5, 10.32) * mm, "end": v(-17.5, -10.32) * mm});
            skLineSegment(sketch, "E193.0.right", {"start": v(-22.5, 10.32) * mm, "end": v(-22.5, -10.32) * mm});
            skLineSegment(sketch, "E194.MirrorCS", {"start": v(22.5, 10.32) * mm, "end": v(22.5, -10.32) * mm});
            skLineSegment(sketch, "E195.MirrorCS", {"start": v(20, 10.32) * mm, "end": v(20, -10.32) * mm, "construction": true});
            skLineSegment(sketch, "E196.MirrorCS", {"start": v(17.5, 10.32) * mm, "end": v(17.5, -10.32) * mm});
            skArc(sketch, "E197.MirrorCS", {"start": v(22.5, 10.32) * mm, "mid": v(20, 12.82) * mm, "end": v(17.5, 10.32) * mm});
            skArc(sketch, "E198.MirrorCS", {"start": v(17.5, -10.32) * mm, "mid": v(20, -12.82) * mm, "end": v(22.5, -10.32) * mm});
            skLineSegment(sketch, "E199", {"start": v(-27.7, 23.4) * mm, "end": v(-27.7, 16.9) * mm, "construction": true});
            skArc(sketch, "E200.0.startCap", {"start": v(-29.2, 23.4) * mm, "mid": v(-27.7, 24.9) * mm, "end": v(-26.2, 23.4) * mm});
            skArc(sketch, "E200.0.endCap", {"start": v(-26.2, 16.9) * mm, "mid": v(-27.7, 15.4) * mm, "end": v(-29.2, 16.9) * mm});
            skLineSegment(sketch, "E200.0.left", {"start": v(-26.2, 23.4) * mm, "end": v(-26.2, 16.9) * mm});
            skLineSegment(sketch, "E200.0.right", {"start": v(-29.2, 23.4) * mm, "end": v(-29.2, 16.9) * mm});
            skArc(sketch, "E201.0.1.0", {"start": v(-26.2, -3.25) * mm, "mid": v(-27.7, -4.75) * mm, "end": v(-29.2, -3.25) * mm});
            skLineSegment(sketch, "E201.0.1.1", {"start": v(-29.2, 3.25) * mm, "end": v(-29.2, -3.25) * mm});
            skArc(sketch, "E201.0.1.2", {"start": v(-29.2, 3.25) * mm, "mid": v(-27.7, 4.75) * mm, "end": v(-26.2, 3.25) * mm});
            skLineSegment(sketch, "E201.0.1.3", {"start": v(-27.7, 3.25) * mm, "end": v(-27.7, -3.25) * mm, "construction": true});
            skLineSegment(sketch, "E201.0.1.4", {"start": v(-26.2, 3.25) * mm, "end": v(-26.2, -3.25) * mm});
            skArc(sketch, "E201.0.2.0", {"start": v(-26.2, -23.4) * mm, "mid": v(-27.7, -24.9) * mm, "end": v(-29.2, -23.4) * mm});
            skLineSegment(sketch, "E201.0.2.1", {"start": v(-29.2, -16.9) * mm, "end": v(-29.2, -23.4) * mm});
            skArc(sketch, "E201.0.2.2", {"start": v(-29.2, -16.9) * mm, "mid": v(-27.7, -15.4) * mm, "end": v(-26.2, -16.9) * mm});
            skLineSegment(sketch, "E201.0.2.3", {"start": v(-27.7, -16.9) * mm, "end": v(-27.7, -23.4) * mm, "construction": true});
            skLineSegment(sketch, "E201.0.2.4", {"start": v(-26.2, -16.9) * mm, "end": v(-26.2, -23.4) * mm});
            skArc(sketch, "E201.1.0.0", {"start": v(29.2, 16.9) * mm, "mid": v(27.7, 15.4) * mm, "end": v(26.2, 16.9) * mm});
            skLineSegment(sketch, "E201.1.0.1", {"start": v(26.2, 23.4) * mm, "end": v(26.2, 16.9) * mm});
            skArc(sketch, "E201.1.0.2", {"start": v(26.2, 23.4) * mm, "mid": v(27.7, 24.9) * mm, "end": v(29.2, 23.4) * mm});
            skLineSegment(sketch, "E201.1.0.3", {"start": v(27.7, 23.4) * mm, "end": v(27.7, 16.9) * mm, "construction": true});
            skLineSegment(sketch, "E201.1.0.4", {"start": v(29.2, 23.4) * mm, "end": v(29.2, 16.9) * mm});
            skArc(sketch, "E201.1.1.0", {"start": v(29.2, -3.25) * mm, "mid": v(27.7, -4.75) * mm, "end": v(26.2, -3.25) * mm});
            skLineSegment(sketch, "E201.1.1.1", {"start": v(26.2, 3.25) * mm, "end": v(26.2, -3.25) * mm});
            skArc(sketch, "E201.1.1.2", {"start": v(26.2, 3.25) * mm, "mid": v(27.7, 4.75) * mm, "end": v(29.2, 3.25) * mm});
            skLineSegment(sketch, "E201.1.1.3", {"start": v(27.7, 3.25) * mm, "end": v(27.7, -3.25) * mm, "construction": true});
            skLineSegment(sketch, "E201.1.1.4", {"start": v(29.2, 3.25) * mm, "end": v(29.2, -3.25) * mm});
            skArc(sketch, "E201.1.2.0", {"start": v(29.2, -23.4) * mm, "mid": v(27.7, -24.9) * mm, "end": v(26.2, -23.4) * mm});
            skLineSegment(sketch, "E201.1.2.1", {"start": v(26.2, -16.9) * mm, "end": v(26.2, -23.4) * mm});
            skArc(sketch, "E201.1.2.2", {"start": v(26.2, -16.9) * mm, "mid": v(27.7, -15.4) * mm, "end": v(29.2, -16.9) * mm});
            skLineSegment(sketch, "E201.1.2.3", {"start": v(27.7, -16.9) * mm, "end": v(27.7, -23.4) * mm, "construction": true});
            skLineSegment(sketch, "E201.1.2.4", {"start": v(29.2, -16.9) * mm, "end": v(29.2, -23.4) * mm});
            skLineSegment(sketch, "E201.direction1", {"start": v(-29.2, 16.9) * mm, "end": v(26.2, 16.9) * mm, "construction": true});
            skLineSegment(sketch, "E201.direction2", {"start": v(-29.2, 16.9) * mm, "end": v(-29.2, -3.25) * mm, "construction": true});
            skPoint(sketch, "E202", {"position": v(-27.7, 0) * mm});
            skSolve(sketch);
        }
        {
            var Q0;
            Q0=makeQuery(id+"F9.imprint","IMPRINT",FACE,{"disambiguationData":[TD([[makeQuery(id+"F9.imprint","IMPRINT",EDGE,{"derivedFrom":sQuery(id+"F9.wireOp",EDGE,"E172.bottom")}),1.0]])]});
            extrude(context, id + "F10", {"entities" : qUnion([Q0]), "depth" : 3 * mm, "offsetDistance" : 25 * mm});
        }
    });
